# Revit family: Sanitary_Shower-Trays_Sanindusa_New-WCCare-Shower-Tray
name_source: partatom
category: Plumbing Fixtures
revit_build: Autodesk Revit 2018 (Build: 20170223_1515(x64)
units: mm (PartAtom-declared; Revit-internal decimal feet)

## family parameters
Always vertical = Yes
Cut with Voids When Loaded = No
OmniClass Number = 23.45.00.00
OmniClass Title = Sanitary, Laundry, and Cleaning Equipment
Part Type = Normal
Room Calculation Point = No
Round Connector Dimension = Use Diameter
Shared = No
Work Plane-Based = No

## types (1)
- Sanitary_Shower-Trays_Sanindusa_New-WCCare-Shower-Tray
    AssetType = Fixed
    CodePerformance = EN 14527:2006 / A1:2010
CL 2
    Color = white
    Constituents = 49911-90 shower tray drain (not included)
    Cost = 0 $
    Description = shower tray
    DrainSize = 90 mm  [stored 0.295276 ft]
    Edition number = 1
    Element Type = SHOWER: Installation or waste water appliance that emits a spray of water to wash the human body (BS6100)
    Features = Built-in shower tray. Easy accessibility to the shower area especially for older people
and people with disability or reduced mobility. Proper for wheel chairs. 
Glazed on all sides, except on the basis of settlement. 
Anti-slip finishing, which increases the independence, safety
and comfort in the showers area, especially children, older people
and people with disability or reduced mobility.
Versatile application and contemporary design, available in color black or grey.
    Finish = gloss
    Installation Instructions = https://www.tec.sanindusa.pt
    InstallationDate = 1900-12-31T23:59:59
    Manufacturer = Sanindusa
    ManufacturerName = Sanindusa
    ManufacturerURL = www.tec.sanindusa.pt
    Material = Acrylic
    ModelNumber = 8009000000
    ModelReference = New Wccare
    Name = Shower tray new wccare 120x90
    NominalHeight = 50 mm  [stored 0.164042 ft]
    NominalLength = 1240 mm  [stored 4.06824 ft]
    NominalWidth = 945 mm  [stored 3.10039 ft]
    Pre-defined type (IFC) = SHOWER
    Product Guid = da444736-b574-4f78-9c72-9aebd2c52acd
    Product data url = https://bimobject.com
    ProductInformation = https://www.tec.sanindusa.pt
    ProductionYear = 2017
    Shape = rectangular
    Size = 120x90
    Type (IFC) = IfcSanitaryTerminalType
    URL = www.tec.sanindusa.pt
    Uniclass2015Code = Pr_40_20_06_84
    Uniclass2015Title = Shower trays
    Uniclass2015Version = Products v1.6
    Version = 2
    WarrantyDescription = https://www.tec.sanindusa.pt
    WarrantyDurationParts = 5
    WarrantyDurationUnit = year
    WarrantyStartDate = 1900-12-31T23:59:59
1900-12-31T23:59:59
    Weight = 22.00 kg

note: [stored X ft] marks values corroborated as IEEE doubles in the binary element streams (Revit-internal decimal feet)

## geometry (parser evidence)
native form markers: Sweep x9
no freeform markers — native parametric forms only
